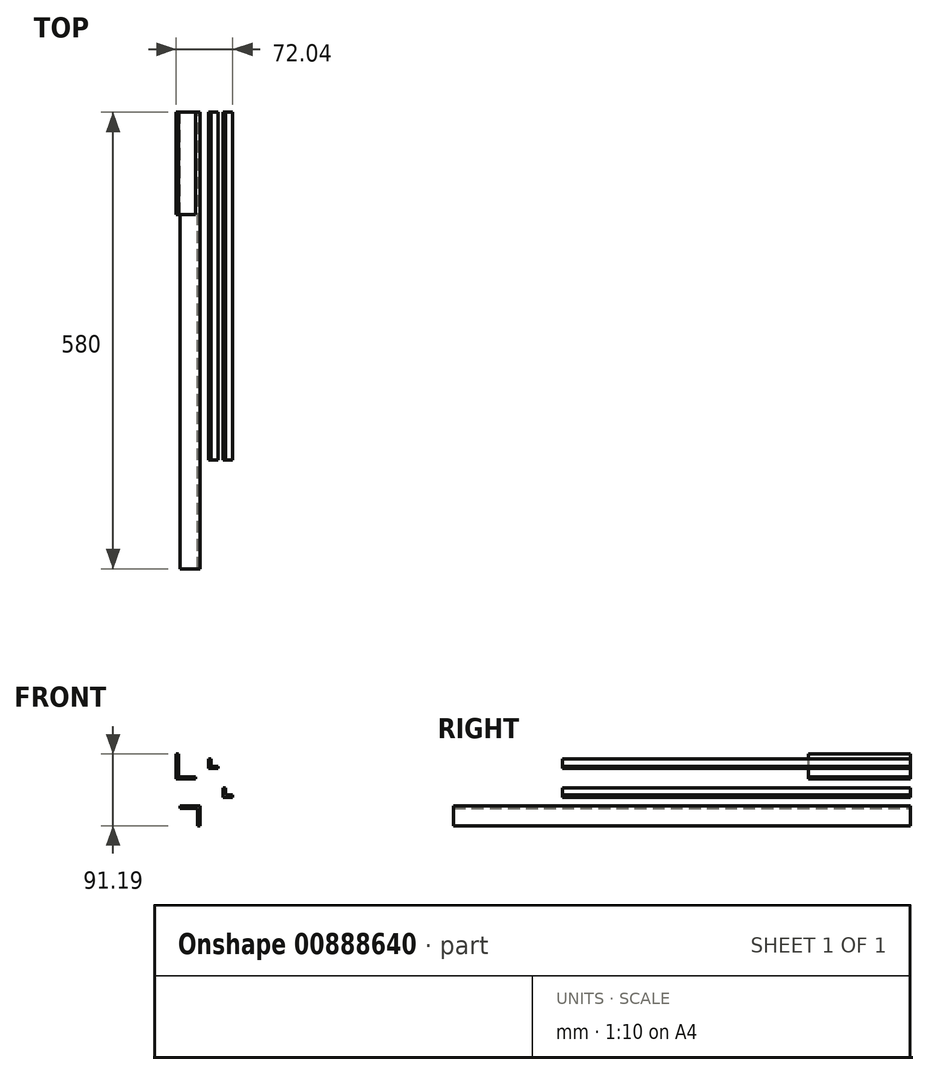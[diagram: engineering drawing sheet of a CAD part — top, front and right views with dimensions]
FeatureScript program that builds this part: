
annotation { "Feature Type Name" : "Feature", "Feature Type Description" : "" }
export const myFeature = defineFeature(function(context is Context, id is Id, definition is map)
    precondition{}
    {
        {
            var Q0;
            Q0=qCreatedBy(makeId("Front.planeOp"),FACE);
            var sketch = newSketch(context, id + "F0", { "sketchPlane" : qUnion([Q0])});
            skLineSegment(sketch, "E0", {"start": v(-60.04, 66.17) * mm, "end": v(-60.04, 34.17) * mm});
            skLineSegment(sketch, "E1", {"start": v(-60.04, 34.17) * mm, "end": v(-35.04, 34.17) * mm});
            skLineSegment(sketch, "E2", {"start": v(-35.04, 34.17) * mm, "end": v(-35.04, 37.17) * mm});
            skLineSegment(sketch, "E3", {"start": v(-35.04, 37.17) * mm, "end": v(-57.04, 37.17) * mm});
            skLineSegment(sketch, "E4", {"start": v(-57.04, 37.17) * mm, "end": v(-57.04, 66.19) * mm});
            skLineSegment(sketch, "E5", {"start": v(-57.04, 66.19) * mm, "end": v(-60.04, 66.17) * mm});
            skSolve(sketch);
        }
        {
            var Q0;
            Q0 = qSketchRegion(id + "F0", true);
            extrude(context, id + "F1", {"entities" : qUnion([Q0]), "depth" : 129.6 * mm, "offsetDistance" : 25 * mm});
        }
        {
            var Q0;
            Q0=qCreatedBy(makeId("Front.planeOp"),FACE);
            var sketch = newSketch(context, id + "F2", { "sketchPlane" : qUnion([Q0])});
            skLineSegment(sketch, "E6", {"start": v(0, 10.9) * mm, "end": v(12, 10.9) * mm});
            skLineSegment(sketch, "E7", {"start": v(12, 10.9) * mm, "end": v(12, 13.9) * mm});
            skLineSegment(sketch, "E8", {"start": v(12, 13.9) * mm, "end": v(3, 13.9) * mm});
            skLineSegment(sketch, "E9", {"start": v(3, 13.9) * mm, "end": v(3, 22.9) * mm});
            skLineSegment(sketch, "E10", {"start": v(3, 22.9) * mm, "end": v(0, 22.9) * mm});
            skLineSegment(sketch, "E11", {"start": v(0, 22.9) * mm, "end": v(0, 10.9) * mm});
            skSolve(sketch);
        }
        {
            var Q0;
            Q0 = qSketchRegion(id + "F2", true);
            extrude(context, id + "F3", {"entities" : qUnion([Q0]), "depth" : 442 * mm, "offsetDistance" : 25 * mm});
        }
        {
            var Q0;
            Q0=qCreatedBy(makeId("Front.planeOp"),FACE);
            var sketch = newSketch(context, id + "F4", { "sketchPlane" : qUnion([Q0])});
            skLineSegment(sketch, "E12", {"start": v(-18.78, 59.5) * mm, "end": v(-18.78, 47.5) * mm});
            skLineSegment(sketch, "E13", {"start": v(-18.78, 47.5) * mm, "end": v(-6.78, 47.5) * mm});
            skLineSegment(sketch, "E14", {"start": v(-6.78, 47.5) * mm, "end": v(-6.78, 50.5) * mm});
            skLineSegment(sketch, "E15", {"start": v(-6.78, 50.5) * mm, "end": v(-15.78, 50.5) * mm});
            skLineSegment(sketch, "E16", {"start": v(-15.78, 50.5) * mm, "end": v(-15.78, 59.5) * mm});
            skLineSegment(sketch, "E17", {"start": v(-15.78, 59.5) * mm, "end": v(-18.78, 59.5) * mm});
            skSolve(sketch);
        }
        {
            var Q0;
            Q0 = qSketchRegion(id + "F4", true);
            extrude(context, id + "F5", {"entities" : qUnion([Q0]), "depth" : 442 * mm, "offsetDistance" : 25 * mm});
        }
        {
            var Q0;
            Q0=qCreatedBy(makeId("Front.planeOp"),FACE);
            var sketch = newSketch(context, id + "F6", { "sketchPlane" : qUnion([Q0])});
            skLineSegment(sketch, "E18", {"start": v(-54.7, 0) * mm, "end": v(-29.7, 0) * mm});
            skLineSegment(sketch, "E19", {"start": v(-29.7, 0) * mm, "end": v(-29.7, -25) * mm});
            skLineSegment(sketch, "E20", {"start": v(-29.7, -25) * mm, "end": v(-32.7, -25) * mm});
            skLineSegment(sketch, "E21", {"start": v(-32.7, -25) * mm, "end": v(-32.7, -3) * mm});
            skLineSegment(sketch, "E22", {"start": v(-32.7, -3) * mm, "end": v(-54.7, -3) * mm});
            skLineSegment(sketch, "E23", {"start": v(-54.7, -3) * mm, "end": v(-54.7, 0) * mm});
            skSolve(sketch);
        }
        {
            var Q0;
            Q0 = qSketchRegion(id + "F6", true);
            extrude(context, id + "F7", {"entities" : qUnion([Q0]), "depth" : 580 * mm, "offsetDistance" : 25 * mm});
        }
    });
